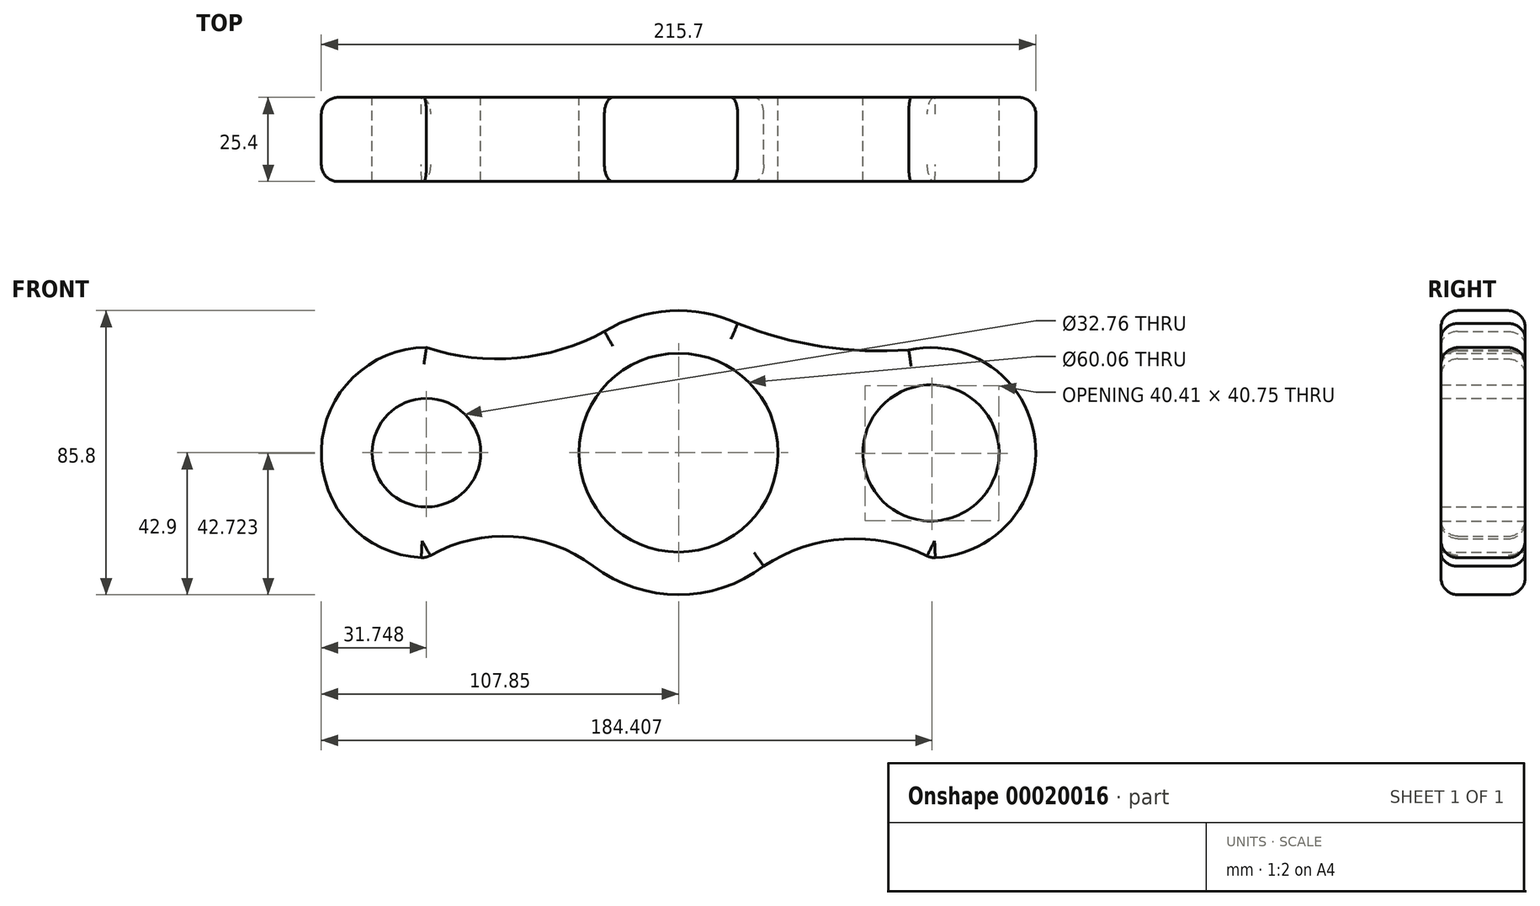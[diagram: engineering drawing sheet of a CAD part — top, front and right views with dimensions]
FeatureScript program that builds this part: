
annotation { "Feature Type Name" : "Feature", "Feature Type Description" : "" }
export const myFeature = defineFeature(function(context is Context, id is Id, definition is map)
    precondition{}
    {
        {
            var Q0;
            Q0=qCreatedBy(makeId("Front.planeOp"),FACE);
            var sketch = newSketch(context, id + "F0", { "sketchPlane" : qUnion([Q0])});
            skCircle(sketch, "E0", {"center": v(0, 0) * mm, "radius": 30.03 * mm});
            skPoint(sketch, "E1", {"position": v(-42.9, 0) * mm});
            skPoint(sketch, "E2", {"position": v(42.9, 0) * mm});
            skLineSegment(sketch, "E3.top", {"start": v(0, 42.78) * mm, "end": v(-3.2, 42.78) * mm});
            skLineSegment(sketch, "E3.left", {"start": v(0, 0) * mm, "end": v(0, 42.78) * mm});
            skLineSegment(sketch, "E4.top", {"start": v(0, 42.78) * mm, "end": v(3.2, 42.78) * mm});
            skPoint(sketch, "E5", {"position": v(0, 42.78) * mm});
            skPoint(sketch, "E6", {"position": v(0, -42.9) * mm});
            skLineSegment(sketch, "E7.bottom", {"start": v(42.9, 0) * mm, "end": v(43.08, 0) * mm});
            skLineSegment(sketch, "E7.left", {"start": v(0, 0) * mm, "end": v(0, -42.9) * mm});
            skLineSegment(sketch, "E8.rect.left", {"start": v(-76.1, -31.75) * mm, "end": v(-76.1, 31.75) * mm});
            skLineSegment(sketch, "E8.rect.right", {"start": v(76.1, -31.75) * mm, "end": v(76.1, 31.75) * mm});
            skCircle(sketch, "E9", {"center": v(-76.1, 0) * mm, "radius": 16.38 * mm});
            skPoint(sketch, "E10", {"position": v(76.1, 0) * mm});
            skArc(sketch, "E11", {"start": v(71.52, 20.15) * mm, "mid": v(63.21, -16.15) * mm, "end": v(96.76, 0) * mm});
            skArc(sketch, "E12", {"start": v(-76.1, 31.75) * mm, "mid": v(-107.85, 0) * mm, "end": v(-76.1, -31.75) * mm});
            skPoint(sketch, "E13", {"position": v(-76.1, 31.75) * mm});
            skPoint(sketch, "E14", {"position": v(-76.1, 16.38) * mm});
            skPoint(sketch, "E15", {"position": v(-76.1, -16.38) * mm});
            skPoint(sketch, "E16", {"position": v(-76.1, -31.75) * mm});
            skArc(sketch, "E17", {"start": v(-76.1, 31.75) * mm, "mid": v(-48.75, 28.6) * mm, "end": v(-22.4, 36.6) * mm});
            skArc(sketch, "E18", {"start": v(-25.8, -34.28) * mm, "mid": v(-50.56, -25.3) * mm, "end": v(-76.1, -31.75) * mm});
            skArc(sketch, "E19.trimOffspring", {"start": v(-25.83, -34.25) * mm, "mid": v(-0.06, -42.9) * mm, "end": v(25.74, -34.32) * mm});
            skArc(sketch, "E20", {"start": v(76.1, -31.75) * mm, "mid": v(107.68, 3.33) * mm, "end": v(69.49, 31.05) * mm});
            skPoint(sketch, "E4.right.end.orphan", {"position": v(42.9, 42.78) * mm});
            skPoint(sketch, "E7.top.end.orphan", {"position": v(43.08, -42.9) * mm});
            skArc(sketch, "E21", {"start": v(76.1, -31.75) * mm, "mid": v(49.37, -26.14) * mm, "end": v(23.79, -35.7) * mm});
            skArc(sketch, "E22", {"start": v(17.85, 39.01) * mm, "mid": v(46.5, 31.6) * mm, "end": v(76.1, 31.75) * mm});
            skArc(sketch, "E23.trimOffspring", {"start": v(17.85, 39.01) * mm, "mid": v(-2.57, 42.82) * mm, "end": v(-22.4, 36.6) * mm});
            skArc(sketch, "E24", {"start": v(96.76, 0) * mm, "mid": v(62.46, 15.19) * mm, "end": v(73.9, -20.54) * mm});
            skPoint(sketch, "E25.orphan", {"position": v(-76.1, 76.1) * mm});
            skPoint(sketch, "E26.orphan", {"position": v(76.1, 76.1) * mm});
            skPoint(sketch, "E8.rect.bottom.end.orphan", {"position": v(76.1, -76.1) * mm});
            skPoint(sketch, "E27.orphan", {"position": v(-76.1, -76.1) * mm});
            skSolve(sketch);
        }
        {
            var Q0;
            Q0 = qSketchRegion(id + "F0", true);
            extrude(context, id + "F1", {"entities" : qUnion([Q0]), "depth" : 25.4 * mm});
        }
        {
            var Q0;
            Q0=makeQuery(id+"F1.opExtrude","CAP_EDGE",EDGE,{"disambiguationData":[OSD([sQuery(id+"F0.wireOp",EDGE,"E12")])],"isStart":false});
            var Q1;
            Q1=makeQuery(id+"F1.opExtrude","CAP_EDGE",EDGE,{"disambiguationData":[OSD([sQuery(id+"F0.wireOp",EDGE,"E18")])],"isStart":false});
            var Q2;
            Q2=makeQuery(id+"F1.opExtrude","CAP_EDGE",EDGE,{"disambiguationData":[OSD([sQuery(id+"F0.wireOp",EDGE,"E12")])],"isStart":true});
            var Q3;
            Q3=makeQuery(id+"F1.opExtrude","CAP_EDGE",EDGE,{"disambiguationData":[OSD([sQuery(id+"F0.wireOp",EDGE,"E18")])],"isStart":true});
            var Q4;
            Q4=makeQuery(id+"F1.opExtrude","CAP_EDGE",EDGE,{"disambiguationData":[OSD([sQuery(id+"F0.wireOp",EDGE,"E19.trimOffspring")])],"isStart":true});
            var Q5;
            Q5=makeQuery(id+"F1.opExtrude","CAP_EDGE",EDGE,{"disambiguationData":[OSD([sQuery(id+"F0.wireOp",EDGE,"E19.trimOffspring")])],"isStart":false});
            var Q6;
            Q6=makeQuery(id+"F1.opExtrude","CAP_EDGE",EDGE,{"disambiguationData":[OSD([sQuery(id+"F0.wireOp",EDGE,"E21")])],"isStart":false});
            var Q7;
            Q7=makeQuery(id+"F1.opExtrude","CAP_EDGE",EDGE,{"disambiguationData":[OSD([sQuery(id+"F0.wireOp",EDGE,"E21")])],"isStart":true});
            var Q8;
            Q8=makeQuery(id+"F1.opExtrude","CAP_EDGE",EDGE,{"disambiguationData":[OSD([sQuery(id+"F0.wireOp",EDGE,"E20")])],"isStart":false});
            var Q9;
            Q9=makeQuery(id+"F1.opExtrude","CAP_EDGE",EDGE,{"disambiguationData":[OSD([sQuery(id+"F0.wireOp",EDGE,"E20")])],"isStart":true});
            var Q10;
            Q10=makeQuery(id+"F1.opExtrude","CAP_EDGE",EDGE,{"disambiguationData":[OSD([sQuery(id+"F0.wireOp",EDGE,"E22")])],"isStart":false});
            var Q11;
            Q11=makeQuery(id+"F1.opExtrude","CAP_EDGE",EDGE,{"disambiguationData":[OSD([sQuery(id+"F0.wireOp",EDGE,"E22")])],"isStart":true});
            var Q12;
            Q12=makeQuery(id+"F1.opExtrude","CAP_EDGE",EDGE,{"disambiguationData":[OSD([sQuery(id+"F0.wireOp",EDGE,"E23.trimOffspring")])],"isStart":false});
            var Q13;
            Q13=makeQuery(id+"F1.opExtrude","CAP_EDGE",EDGE,{"disambiguationData":[OSD([sQuery(id+"F0.wireOp",EDGE,"E23.trimOffspring")])],"isStart":true});
            var Q14;
            Q14=makeQuery(id+"F1.opExtrude","CAP_EDGE",EDGE,{"disambiguationData":[OSD([sQuery(id+"F0.wireOp",EDGE,"E17")])],"isStart":true});
            var Q15;
            Q15=makeQuery(id+"F1.opExtrude","CAP_EDGE",EDGE,{"disambiguationData":[OSD([sQuery(id+"F0.wireOp",EDGE,"E17")])],"isStart":false});
            fillet(context, id + "F2", {"entities" : qUnion([Q0, Q1, Q2, Q3, Q4, Q5, Q6, Q7, Q8, Q9, Q10, Q11, Q12, Q13, Q14, Q15]), "radius" : 5.08 * mm, "tangentPropagation" : true, "allowEdgeOverflow" : false});
        }
        {
            var Q0;
            Q0=makeQuery(id+"F1.opExtrude","SWEPT_EDGE",EDGE,{"disambiguationData":[OSD([sQuery(id+"F0.wireOp",EDGE,"E8.rect.left"),sQuery(id+"F0.wireOp",EDGE,"E12"),sQuery(id+"F0.wireOp",EDGE,"E18")])]});
            fillet(context, id + "F3", {"entities" : qUnion([Q0]), "radius" : 5.08 * mm, "tangentPropagation" : true, "allowEdgeOverflow" : false});
        }
        {
            var Q0;
            Q0=makeQuery(id+"F1.opExtrude","SWEPT_EDGE",EDGE,{"disambiguationData":[OSD([sQuery(id+"F0.wireOp",EDGE,"E8.rect.right"),sQuery(id+"F0.wireOp",EDGE,"E20"),sQuery(id+"F0.wireOp",EDGE,"E21")])]});
            fillet(context, id + "F4", {"entities" : qUnion([Q0]), "radius" : 5.08 * mm, "tangentPropagation" : true, "allowEdgeOverflow" : false});
        }
    });
